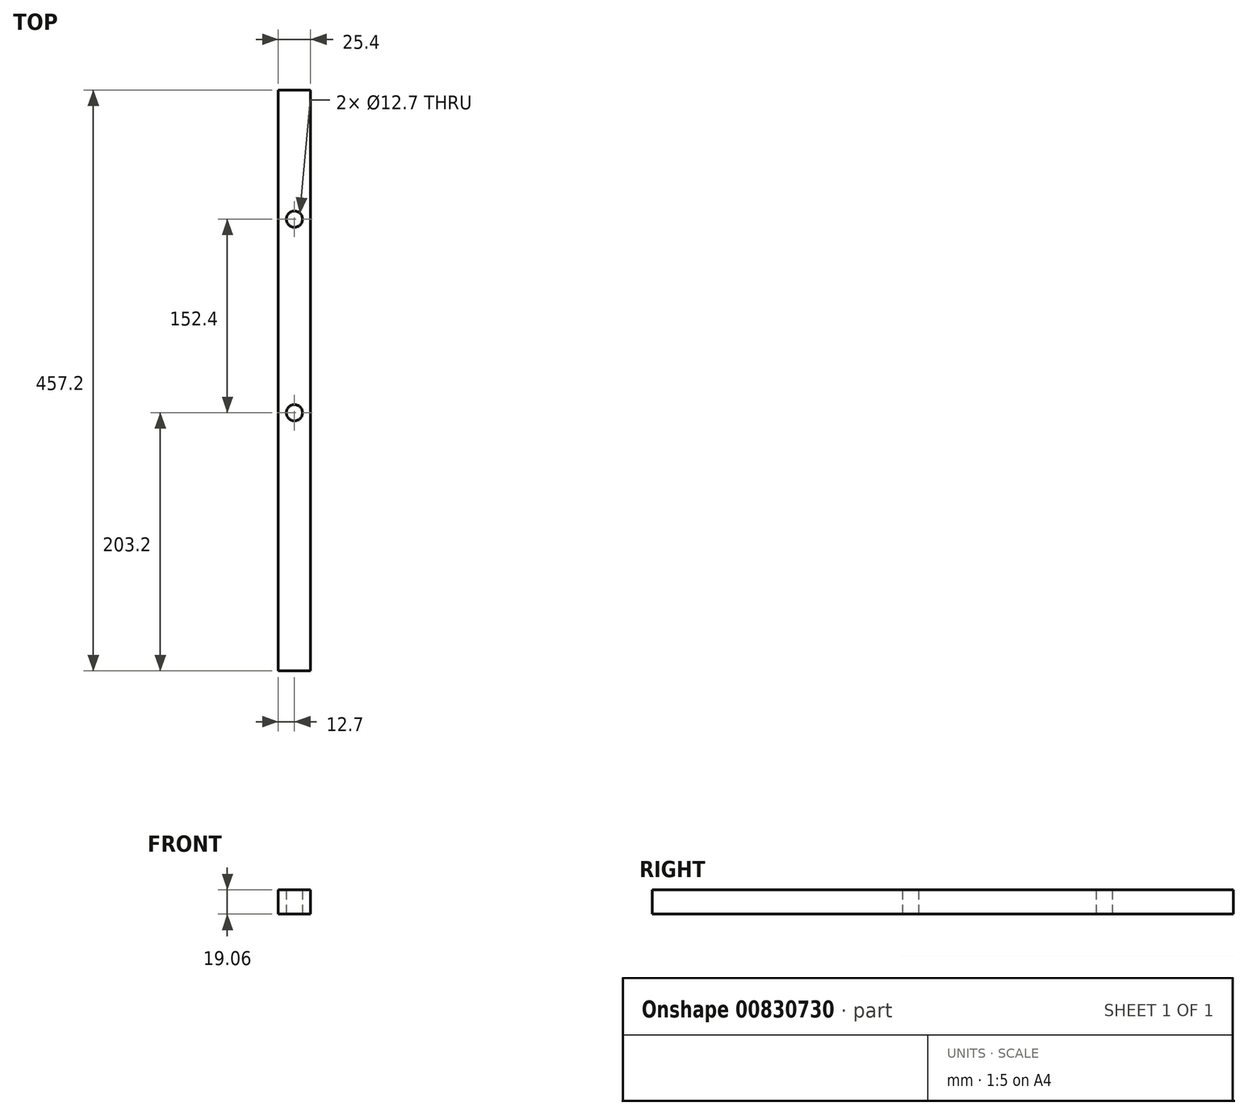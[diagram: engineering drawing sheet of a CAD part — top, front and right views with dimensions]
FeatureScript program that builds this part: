
annotation { "Feature Type Name" : "Feature", "Feature Type Description" : "" }
export const myFeature = defineFeature(function(context is Context, id is Id, definition is map)
    precondition{}
    {
        {
            var Q0;
            Q0=qCreatedBy(makeId("Front.planeOp"),FACE);
            var sketch = newSketch(context, id + "F0", { "sketchPlane" : qUnion([Q0])});
            skLineSegment(sketch, "E0.bottom", {"start": v(12.7, -9.53) * mm, "end": v(-12.7, -9.53) * mm});
            skLineSegment(sketch, "E0.top", {"start": v(12.7, 9.52) * mm, "end": v(-12.7, 9.52) * mm});
            skLineSegment(sketch, "E0.left", {"start": v(12.7, -9.53) * mm, "end": v(12.7, 9.52) * mm});
            skLineSegment(sketch, "E0.right", {"start": v(-12.7, -9.53) * mm, "end": v(-12.7, 9.52) * mm});
            skPoint(sketch, "E0.middle", {"position": v(0, 0) * mm});
            skSolve(sketch);
        }
        {
            var Q0;
            Q0 = qSketchRegion(id + "F0", true);
            extrude(context, id + "F1", {"entities" : qUnion([Q0]), "depth" : 457.2 * mm, "offsetDistance" : 25.4 * mm});
        }
        {
            var Q0;
            Q0=makeQuery(id+"F1.opExtrude","SWEPT_FACE",FACE,{"disambiguationData":[OSD([sQuery(id+"F0.wireOp",EDGE,"E0.bottom")])]});
            var sketch = newSketch(context, id + "F2", { "sketchPlane" : qUnion([Q0])});
            skCircle(sketch, "E1", {"center": v(0, 254) * mm, "radius": 6.35 * mm});
            skLineSegment(sketch, "E2", {"start": v(0, 0) * mm, "end": v(0, 342.9) * mm, "construction": true});
            skCircle(sketch, "E3", {"center": v(0, 101.6) * mm, "radius": 6.35 * mm});
            skSolve(sketch);
        }
        {
            var Q0;
            Q0 = qSketchRegion(id + "F2", true);
            extrude(context, id + "F3", {"entities" : qUnion([Q0]), "operationType" : NewBodyOperationType.REMOVE, "endBound" : BoundingType.THROUGH_ALL, "oppositeDirection" : true, "depth" : 25.4 * mm, "offsetDistance" : 25.4 * mm});
        }
    });
